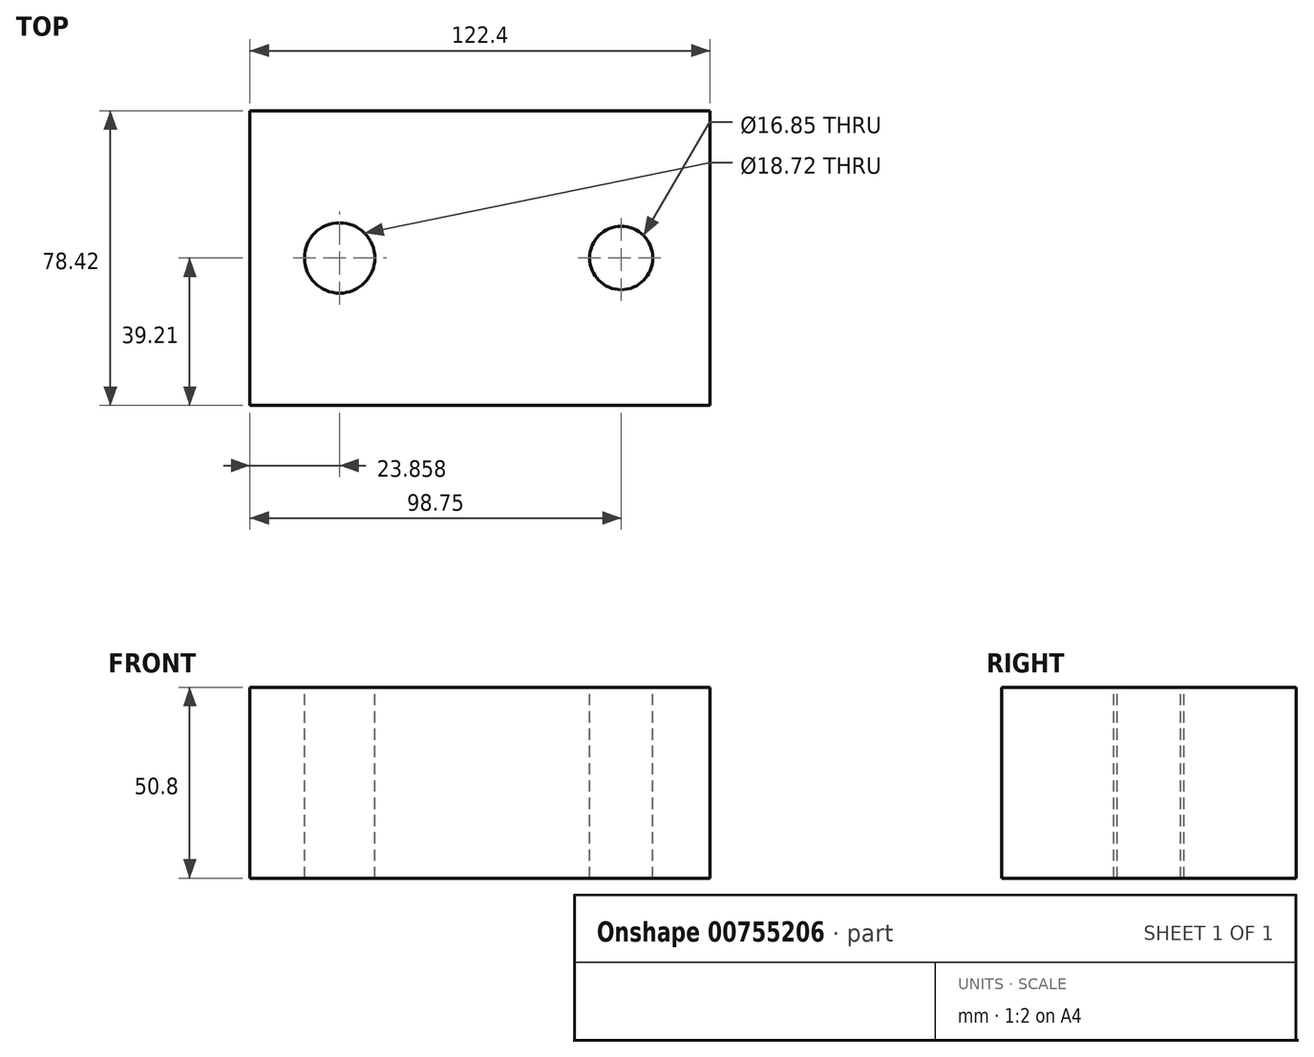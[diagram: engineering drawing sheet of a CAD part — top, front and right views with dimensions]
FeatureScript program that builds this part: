
annotation { "Feature Type Name" : "Feature", "Feature Type Description" : "" }
export const myFeature = defineFeature(function(context is Context, id is Id, definition is map)
    precondition{}
    {
        {
            var Q0;
            Q0=qCreatedBy(makeId("Top.planeOp"),FACE);
            var sketch = newSketch(context, id + "F0", { "sketchPlane" : qUnion([Q0])});
            skLineSegment(sketch, "E0.bottom", {"start": v(61.2, -39.2) * mm, "end": v(-61.2, -39.2) * mm});
            skLineSegment(sketch, "E0.top", {"start": v(61.2, 39.2) * mm, "end": v(-61.2, 39.2) * mm});
            skLineSegment(sketch, "E0.left", {"start": v(61.2, -39.2) * mm, "end": v(61.2, 39.2) * mm});
            skLineSegment(sketch, "E0.right", {"start": v(-61.2, -39.2) * mm, "end": v(-61.2, 39.2) * mm});
            skPoint(sketch, "E0.middle", {"position": v(0, 0) * mm});
            skSolve(sketch);
        }
        {
            var Q0;
            Q0=makeQuery(id+"F0.imprint","IMPRINT",FACE,{"disambiguationData":[TD([[makeQuery(id+"F0.imprint","IMPRINT",EDGE,{"derivedFrom":sQuery(id+"F0.wireOp",EDGE,"E0.bottom")}),-1.0]])]});
            extrude(context, id + "F1", {"entities" : qUnion([Q0]), "depth" : 50.8 * mm, "offsetDistance" : 25.4 * mm});
        }
        {
            var Q0;
            Q0=qCreatedBy(makeId("Top.planeOp"),FACE);
            var sketch = newSketch(context, id + "F2", { "sketchPlane" : qUnion([Q0])});
            skCircle(sketch, "E1", {"center": v(-37.34, 0) * mm, "radius": 9.36 * mm});
            skCircle(sketch, "E2", {"center": v(37.55, 0) * mm, "radius": 8.42 * mm});
            skSolve(sketch);
        }
        {
            var Q0;
            Q0=makeQuery(id+"F2.imprint","IMPRINT",FACE,{"disambiguationData":[TD([[makeQuery(id+"F2.imprint","IMPRINT",EDGE,{"derivedFrom":sQuery(id+"F2.wireOp",EDGE,"E1")}),1.0]])]});
            var Q1;
            Q1=makeQuery(id+"F2.imprint","IMPRINT",FACE,{"disambiguationData":[TD([[makeQuery(id+"F2.imprint","IMPRINT",EDGE,{"derivedFrom":sQuery(id+"F2.wireOp",EDGE,"E2")}),1.0]])]});
            extrude(context, id + "F3", {"entities" : qUnion([Q0, Q1]), "operationType" : NewBodyOperationType.ADD, "depth" : 101.6 * mm, "offsetDistance" : 25.4 * mm});
        }
        {
            var Q0;
            Q0=makeQuery(id+"F3.opExtrude","CAP_FACE",FACE,{"disambiguationData":[OSD([sQuery(id+"F2.wireOp",EDGE,"E1")])],"isStart":false});
            var Q1;
            Q1=makeQuery(id+"F3.opExtrude","CAP_FACE",FACE,{"disambiguationData":[OSD([sQuery(id+"F2.wireOp",EDGE,"E2")])],"isStart":false});
            extrude(context, id + "F4", {"entities" : qUnion([Q0, Q1]), "operationType" : NewBodyOperationType.REMOVE, "oppositeDirection" : true, "depth" : 101.6 * mm, "offsetDistance" : 25.4 * mm});
        }
    });
